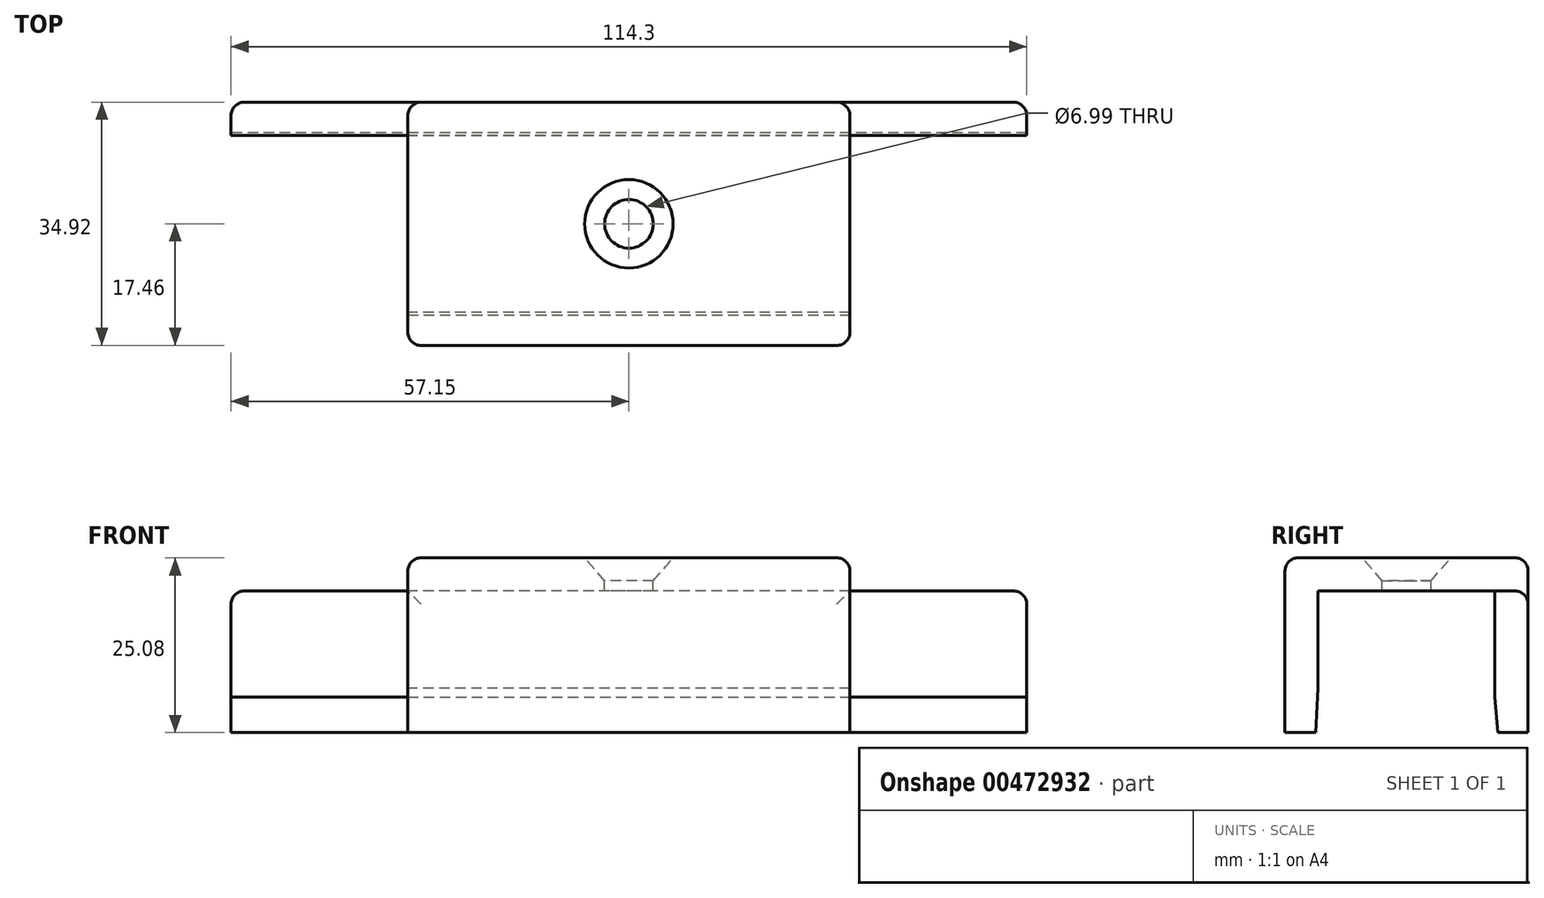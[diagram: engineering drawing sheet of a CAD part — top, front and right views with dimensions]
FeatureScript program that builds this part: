
annotation { "Feature Type Name" : "Feature", "Feature Type Description" : "" }
export const myFeature = defineFeature(function(context is Context, id is Id, definition is map)
    precondition{}
    {
        {
            var Q0;
            Q0=qCreatedBy(makeId("Right.planeOp"),FACE);
            var sketch = newSketch(context, id + "F0", { "sketchPlane" : qUnion([Q0])});
            skLineSegment(sketch, "E0.top", {"start": v(-12.7, 20.32) * mm, "end": v(12.7, 20.32) * mm});
            skLineSegment(sketch, "E0.left", {"start": v(-12.7, 0) * mm, "end": v(-12.7, 20.32) * mm});
            skLineSegment(sketch, "E0.right", {"start": v(12.7, 0) * mm, "end": v(12.7, 20.32) * mm});
            skLineSegment(sketch, "E1.bottom", {"start": v(-17.46, 0) * mm, "end": v(-12.7, 0) * mm});
            skLineSegment(sketch, "E1.top", {"start": v(-17.46, 25.08) * mm, "end": v(17.46, 25.08) * mm});
            skLineSegment(sketch, "E1.left", {"start": v(-17.46, 0) * mm, "end": v(-17.46, 25.08) * mm});
            skLineSegment(sketch, "E1.right", {"start": v(17.46, 0) * mm, "end": v(17.46, 25.08) * mm});
            skLineSegment(sketch, "E2.trimOffspring", {"start": v(12.7, 0) * mm, "end": v(17.46, 0) * mm});
            skSolve(sketch);
        }
        {
            var Q0;
            Q0=makeQuery(id+"F0.imprint","IMPRINT",FACE,{"disambiguationData":[TD([[makeQuery(id+"F0.imprint","IMPRINT",EDGE,{"derivedFrom":sQuery(id+"F0.wireOp",EDGE,"E0.top")}),1.0]])]});
            extrude(context, id + "F1", {"entities" : qUnion([Q0]), "endBound" : BoundingType.SYMMETRIC, "depth" : 63.5 * mm});
        }
        {
            var Q0;
            Q0=makeQuery(id+"F1.opExtrude","CAP_FACE",FACE,{"disambiguationData":[OSD([sQuery(id+"F0.wireOp",EDGE,"E0.top"),sQuery(id+"F0.wireOp",EDGE,"E0.left"),sQuery(id+"F0.wireOp",EDGE,"E0.right"),sQuery(id+"F0.wireOp",EDGE,"E1.bottom"),sQuery(id+"F0.wireOp",EDGE,"E1.top"),sQuery(id+"F0.wireOp",EDGE,"E1.left"),sQuery(id+"F0.wireOp",EDGE,"E1.right"),sQuery(id+"F0.wireOp",EDGE,"E2.trimOffspring")])],"isStart":true});
            var sketch = newSketch(context, id + "F2", { "sketchPlane" : qUnion([Q0])});
            skLineSegment(sketch, "E3.top", {"start": v(-17.46, 0) * mm, "end": v(-12.7, 0) * mm});
            skLineSegment(sketch, "E3.left", {"start": v(-17.46, 20.32) * mm, "end": v(-17.46, 0) * mm});
            skLineSegment(sketch, "E3.right", {"start": v(-12.7, 20.32) * mm, "end": v(-12.7, 0) * mm});
            skLineSegment(sketch, "E4", {"start": v(-12.7, 20.32) * mm, "end": v(-17.46, 20.32) * mm});
            skSolve(sketch);
        }
        {
            var Q0;
            Q0=makeQuery(id+"F9ZKkDRhOTEdfLM_1.boolean.opBoolean","MERGE",FACE,{"derivedFrom":[makeQuery(id+"F1.opExtrude","SWEPT_FACE",FACE,{"disambiguationData":[OSD([sQuery(id+"F0.wireOp",EDGE,"E1.top")])]}),makeQuery(id+"F9ZKkDRhOTEdfLM_1.opExtrude","SWEPT_FACE",FACE,{"disambiguationData":[OSD([sQuery(id+"F2.wireOp",EDGE,"E3.bottom")])]})]});
            var sketch = newSketch(context, id + "F3", { "sketchPlane" : qUnion([Q0])});
            skPoint(sketch, "E5", {"position": v(0, 0) * mm});
            skSolve(sketch);
        }
        {
            var Q0;
            Q0=sQuery(id+"F3.wireOp",VERTEX,"E5");
            var Q1;
            Q1=makeQuery(id+"F1.opExtrude","SWEPT_BODY",BODY,{"disambiguationData":[OSD([sQuery(id+"F0.wireOp",EDGE,"E0.top"),sQuery(id+"F0.wireOp",EDGE,"E0.left"),sQuery(id+"F0.wireOp",EDGE,"E0.right"),sQuery(id+"F0.wireOp",EDGE,"E1.bottom"),sQuery(id+"F0.wireOp",EDGE,"E1.top"),sQuery(id+"F0.wireOp",EDGE,"E1.left"),sQuery(id+"F0.wireOp",EDGE,"E1.right"),sQuery(id+"F0.wireOp",EDGE,"E2.trimOffspring")])]});
            hole(context, id + "F4", {"style" : HoleStyle.C_SINK, "endStyle" : HoleEndStyle.BLIND, "holeDiameter" : 7 * mm, "cSinkDiameter" : 12.7 * mm, "cSinkAngle" : 82 * degree, "holeDepth" : 12.7 * mm, "isTappedThrough" : true, "tappedDepth" : 12.7 * mm, "tapClearance" : 3, "locations" : qUnion([Q0]), "scope" : qUnion([Q1])});
        }
        {
            var Q0;
            Q0=makeQuery(id+"F1.opExtrude","SWEPT_EDGE",EDGE,{"disambiguationData":[OSD([sQuery(id+"F0.wireOp",EDGE,"E0.left"),sQuery(id+"F0.wireOp",EDGE,"E1.bottom")])]});
            chamfer(context, id + "F5", {"entities" : qUnion([Q0]), "chamferType" : ChamferType.TWO_OFFSETS, "width1" : 6.35 * mm, "oppositeDirection" : false, "width2" : 0.38 * mm, "tangentPropagation" : true});
        }
        {
            var Q0;
            Q0=makeQuery(id+"F2.imprint","IMPRINT",FACE,{"disambiguationData":[TD([[makeQuery(id+"F2.imprint","IMPRINT",EDGE,{"derivedFrom":sQuery(id+"F2.wireOp",EDGE,"E3.top")}),-1.0]])]});
            extrude(context, id + "F6", {"entities" : qUnion([Q0]), "operationType" : NewBodyOperationType.ADD, "depth" : 25.4 * mm});
        }
        {
            var Q0;
            Q0=makeQuery(id+"F6.boolean.opBoolean","MERGE",EDGE,{"derivedFrom":[makeQuery(id+"F1.opExtrude","SWEPT_EDGE",EDGE,{"disambiguationData":[OSD([sQuery(id+"F0.wireOp",EDGE,"E0.right"),sQuery(id+"F0.wireOp",EDGE,"E2.trimOffspring")])]}),makeQuery(id+"F6.opExtrude","SWEPT_EDGE",EDGE,{"disambiguationData":[OSD([sQuery(id+"F2.wireOp",EDGE,"E3.top"),sQuery(id+"F2.wireOp",EDGE,"E3.right")])]})]});
            chamfer(context, id + "F7", {"entities" : qUnion([Q0]), "chamferType" : ChamferType.TWO_OFFSETS, "width1" : 0.38 * mm, "oppositeDirection" : false, "width2" : 5.08 * mm, "tangentPropagation" : true});
        }
        {
            var Q0;
            Q0=makeQuery(id+"F1.opExtrude","CAP_EDGE",EDGE,{"disambiguationData":[OSD([sQuery(id+"F0.wireOp",EDGE,"E1.top")])],"isStart":true});
            var Q1;
            Q1=makeQuery(id+"F6.opExtrude","CAP_EDGE",EDGE,{"disambiguationData":[OSD([sQuery(id+"F2.wireOp",EDGE,"E4")])],"isStart":true});
            var Q2;
            Q2=makeQuery(id+"F6.opExtrude","CAP_EDGE",EDGE,{"disambiguationData":[OSD([sQuery(id+"F2.wireOp",EDGE,"E4")])],"isStart":false});
            var Q3;
            Q3=makeQuery(id+"F1.opExtrude","CAP_EDGE",EDGE,{"disambiguationData":[OSD([sQuery(id+"F0.wireOp",EDGE,"E1.top")])],"isStart":false});
            var Q4;
            Q4=makeQuery(id+"F1.opExtrude","SWEPT_EDGE",EDGE,{"disambiguationData":[OSD([sQuery(id+"F0.wireOp",EDGE,"E1.top"),sQuery(id+"F0.wireOp",EDGE,"E1.right")])]});
            var Q5;
            Q5=makeQuery(id+"F1.opExtrude","CAP_EDGE",EDGE,{"disambiguationData":[OSD([sQuery(id+"F0.wireOp",EDGE,"E1.right")])],"isStart":true});
            var Q6;
            Q6=makeQuery(id+"F6.opExtrude","SWEPT_EDGE",EDGE,{"disambiguationData":[OSD([sQuery(id+"F0.wireOp",EDGE,"E1.right"),sQuery(id+"F2.wireOp",EDGE,"E3.left"),sQuery(id+"F2.wireOp",EDGE,"E4")])]});
            var Q7;
            Q7=makeQuery(id+"F1.opExtrude","SWEPT_EDGE",EDGE,{"disambiguationData":[OSD([sQuery(id+"F0.wireOp",EDGE,"E1.top"),sQuery(id+"F0.wireOp",EDGE,"E1.left")])]});
            fillet(context, id + "F8", {"entities" : qUnion([Q0, Q1, Q2, Q3, Q4, Q5, Q6, Q7]), "radius" : 1.9 * mm, "tangentPropagation" : true, "allowEdgeOverflow" : false});
        }
        {
            var Q0;
            Q0=makeQuery(id+"F6.opExtrude","CAP_EDGE",EDGE,{"disambiguationData":[OSD([sQuery(id+"F2.wireOp",EDGE,"E3.left")])],"isStart":false});
            var Q1;
            Q1=makeQuery(id+"F1.opExtrude","CAP_EDGE",EDGE,{"disambiguationData":[OSD([sQuery(id+"F0.wireOp",EDGE,"E1.right")])],"isStart":false});
            var Q2;
            Q2=makeQuery(id+"F1.opExtrude","CAP_EDGE",EDGE,{"disambiguationData":[OSD([sQuery(id+"F0.wireOp",EDGE,"E1.left")])],"isStart":true});
            var Q3;
            Q3=makeQuery(id+"F1.opExtrude","CAP_EDGE",EDGE,{"disambiguationData":[OSD([sQuery(id+"F0.wireOp",EDGE,"E1.left")])],"isStart":false});
            fillet(context, id + "F9", {"entities" : qUnion([Q0, Q1, Q2, Q3]), "radius" : 1.9 * mm, "tangentPropagation" : true, "allowEdgeOverflow" : false});
        }
        {
            var Q0;
            Q0=makeQuery(id+"F1.opExtrude","SWEPT_BODY",BODY,{"disambiguationData":[OSD([sQuery(id+"F0.wireOp",EDGE,"E0.top"),sQuery(id+"F0.wireOp",EDGE,"E0.left"),sQuery(id+"F0.wireOp",EDGE,"E0.right"),sQuery(id+"F0.wireOp",EDGE,"E1.bottom"),sQuery(id+"F0.wireOp",EDGE,"E1.top"),sQuery(id+"F0.wireOp",EDGE,"E1.left"),sQuery(id+"F0.wireOp",EDGE,"E1.right"),sQuery(id+"F0.wireOp",EDGE,"E2.trimOffspring")])]});
            var Q1;
            Q1=qCreatedBy(makeId("Right.planeOp"),FACE);
            mirror(context, id + "F10", {"operationType" : NewBodyOperationType.ADD, "entities" : qUnion([Q0]), "mirrorPlane" : qUnion([Q1])});
        }
    });
